# Revit family: Planter_Elevated_CityScapes
name_source: partatom
category: Generic Models
units: mm (PartAtom-declared; Revit-internal decimal feet)

## family parameters
Always vertical = Yes
Can host rebar = No
Cut with Voids When Loaded = No
Part Type = Normal
Room Calculation Point = No
Round Connector Dimension = Use Diameter
Shared = No
Work Plane-Based = No

## types (4) — shared parameters
CAD Details = https://www.arcat.com
Default Elevation = 0' - 0"
Fascia_Depth = 0' - 0 5/8"
Keynote = 32 94 33
Manufacturer = Envisor
Material = <By Category>
PL_FrameThickness = 0' - 2"
Product Page URL = https://www.arcat.com
Specification = https://www.arcat.com
URL = https://cityscapesinc.com
VoidDepth = 0' - 0 1/4"

## per-type parameters (varying)
| type | PL_Height | PL_LegHeight | PL_Length | PL_Width | Trim_Depth | Trim_Width |
| 24 X 60 X34 | 1' - 8" | 1' - 2" | 5' - 0" | 2' - 0" | 0' - 0 3/4" | 0' - 4" |
| 24 X 48 X 34 | 2' - 0" | 1' - 0" | 1' - 6" | 4' - 0" | 0' - 0 3/4" | 0' - 4" |
| 18 X 48 X 34 | 1' - 8" | 1' - 2" | 4' - 0" | 1' - 6" | 0' - 0 3/4" | 0' - 4" |
| 24 X 72 X 34 | 1' - 8" | 1' - 2" | 6' - 0" | 2' - 0" | 0' - 2" | 0' - 3" |

## geometry (parser evidence)
native form markers: Sweep x3
no freeform markers — native parametric forms only
